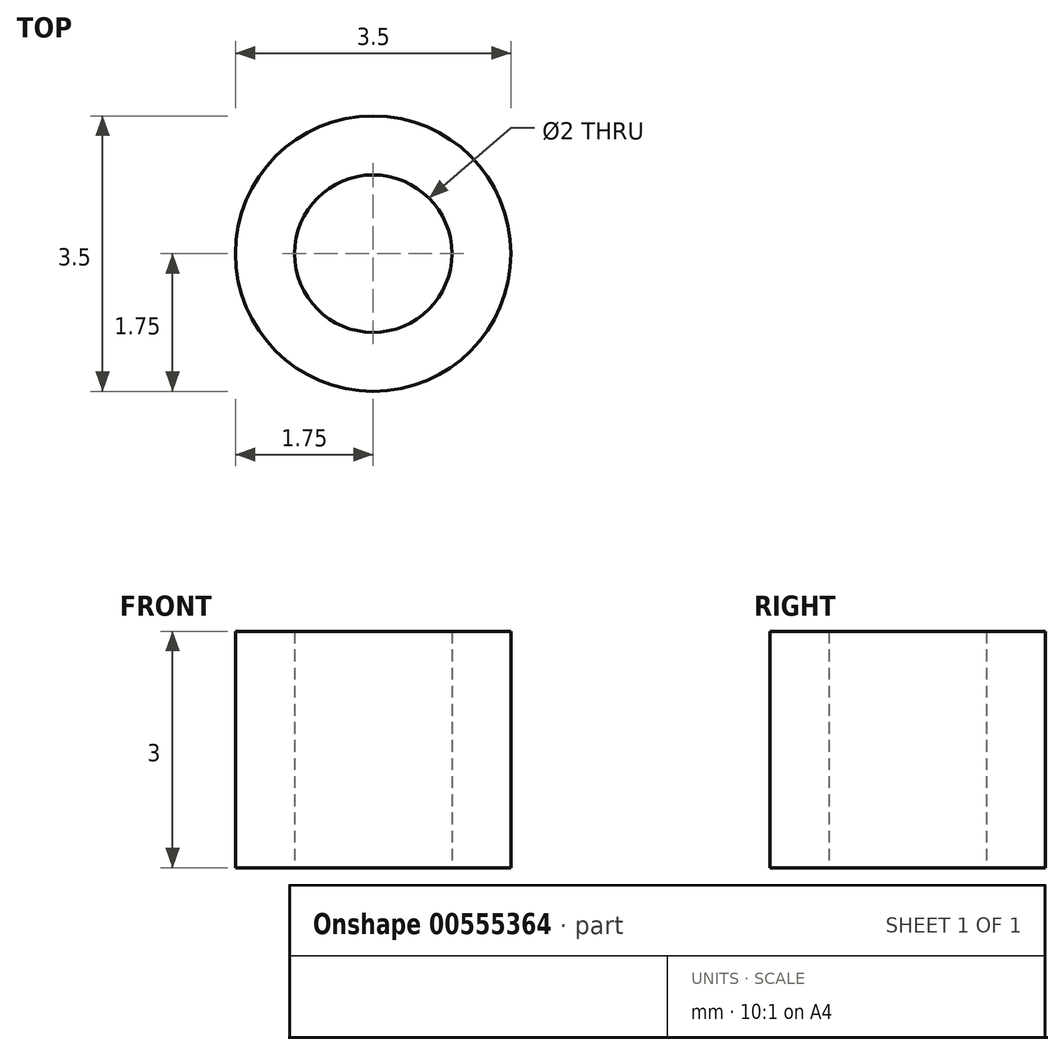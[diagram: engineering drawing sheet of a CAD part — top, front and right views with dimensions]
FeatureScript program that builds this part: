
annotation { "Feature Type Name" : "Feature", "Feature Type Description" : "" }
export const myFeature = defineFeature(function(context is Context, id is Id, definition is map)
    precondition{}
    {
        {
            var Q0;
            Q0=qCreatedBy(makeId("Top.planeOp"),FACE);
            var sketch = newSketch(context, id + "F0", { "sketchPlane" : qUnion([Q0])});
            skCircle(sketch, "E0", {"center": v(0, 0) * mm, "radius": 1 * mm});
            skCircle(sketch, "E1", {"center": v(0, 0) * mm, "radius": 1.75 * mm});
            skSolve(sketch);
        }
        {
            var Q0;
            Q0 = qSketchRegion(id + "F0", true);
            extrude(context, id + "F1", {"entities" : qUnion([Q0]), "depth" : 3 * mm, "offsetDistance" : 25 * mm});
        }
    });
